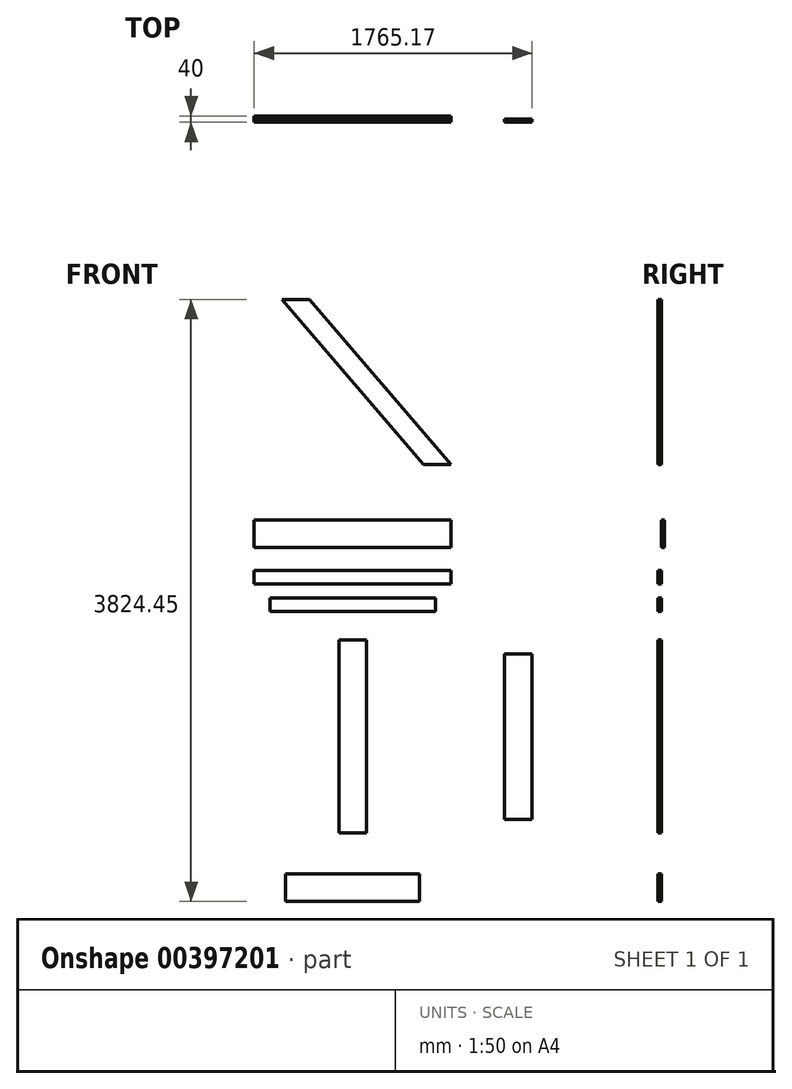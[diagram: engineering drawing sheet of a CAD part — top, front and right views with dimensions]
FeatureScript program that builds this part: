
annotation { "Feature Type Name" : "Feature", "Feature Type Description" : "" }
export const myFeature = defineFeature(function(context is Context, id is Id, definition is map)
    precondition{}
    {
        {
            var Q0;
            Q0=qCreatedBy(makeId("Front.planeOp"),FACE);
            var sketch = newSketch(context, id + "F0", { "sketchPlane" : qUnion([Q0])});
            skLineSegment(sketch, "E0.bottom", {"start": v(625, 87.5) * mm, "end": v(-625, 87.5) * mm});
            skLineSegment(sketch, "E0.top", {"start": v(625, -87.5) * mm, "end": v(-625, -87.5) * mm});
            skLineSegment(sketch, "E0.left", {"start": v(625, 87.5) * mm, "end": v(625, -87.5) * mm});
            skLineSegment(sketch, "E0.right", {"start": v(-625, 87.5) * mm, "end": v(-625, -87.5) * mm});
            skPoint(sketch, "E0.middle", {"position": v(0, 0) * mm});
            skSolve(sketch);
        }
        {
            var Q0;
            Q0 = qSketchRegion(id + "F0", true);
            extrude(context, id + "F1", {"entities" : qUnion([Q0]), "depth" : 20 * mm});
        }
        {
            var Q0;
            Q0=makeQuery(id+"F1.opExtrude","CAP_FACE",FACE,{"disambiguationData":[OSD([sQuery(id+"F0.wireOp",EDGE,"E0.bottom"),sQuery(id+"F0.wireOp",EDGE,"E0.top"),sQuery(id+"F0.wireOp",EDGE,"E0.left"),sQuery(id+"F0.wireOp",EDGE,"E0.right")])],"isStart":false});
            var sketch = newSketch(context, id + "F2", { "sketchPlane" : qUnion([Q0])});
            skLineSegment(sketch, "E1.bottom", {"start": v(625, -232.76) * mm, "end": v(-625, -232.76) * mm});
            skLineSegment(sketch, "E1.top", {"start": v(625, -320.26) * mm, "end": v(-625, -320.26) * mm});
            skLineSegment(sketch, "E1.left", {"start": v(625, -232.76) * mm, "end": v(625, -320.26) * mm});
            skLineSegment(sketch, "E1.right", {"start": v(-625, -232.76) * mm, "end": v(-625, -320.26) * mm});
            skPoint(sketch, "E1.middle", {"position": v(0, -276.5) * mm});
            skLineSegment(sketch, "E2.bottom", {"start": v(525, -407.33) * mm, "end": v(-525, -407.33) * mm});
            skLineSegment(sketch, "E2.top", {"start": v(525, -494.83) * mm, "end": v(-525, -494.83) * mm});
            skLineSegment(sketch, "E2.left", {"start": v(525, -407.33) * mm, "end": v(525, -494.83) * mm});
            skLineSegment(sketch, "E2.right", {"start": v(-525, -407.33) * mm, "end": v(-525, -494.83) * mm});
            skPoint(sketch, "E2.middle", {"position": v(0, -451.08) * mm});
            skPoint(sketch, "E2.middle.positionSnap0", {"position": v(0, -320.26) * mm});
            skPoint(sketch, "E2.centerSnap0", {"position": v(0, -320.26) * mm});
            skSolve(sketch);
        }
        {
            var Q0;
            Q0=makeQuery(id+"F2.imprint","IMPRINT",FACE,{"disambiguationData":[TD([[makeQuery(id+"F2.imprint","IMPRINT",EDGE,{"derivedFrom":sQuery(id+"F2.wireOp",EDGE,"E1.bottom")}),1.0]])]});
            var Q1;
            Q1=makeQuery(id+"F2.imprint","IMPRINT",FACE,{"disambiguationData":[TD([[makeQuery(id+"F2.imprint","IMPRINT",EDGE,{"derivedFrom":sQuery(id+"F2.wireOp",EDGE,"E2.bottom")}),1.0]])]});
            extrude(context, id + "F3", {"entities" : qUnion([Q0, Q1]), "depth" : 20 * mm});
        }
        {
            var Q0;
            Q0=makeQuery(id+"F1.opExtrude","CAP_FACE",FACE,{"disambiguationData":[OSD([sQuery(id+"F0.wireOp",EDGE,"E0.bottom"),sQuery(id+"F0.wireOp",EDGE,"E0.top"),sQuery(id+"F0.wireOp",EDGE,"E0.left"),sQuery(id+"F0.wireOp",EDGE,"E0.right")])],"isStart":false});
            var sketch = newSketch(context, id + "F4", { "sketchPlane" : qUnion([Q0])});
            skLineSegment(sketch, "E3.bottom", {"start": v(-450, 438.15) * mm, "end": v(625, 438.15) * mm, "construction": true});
            skLineSegment(sketch, "E3.top", {"start": v(-450, 1488.15) * mm, "end": v(625, 1488.15) * mm, "construction": true});
            skLineSegment(sketch, "E3.left", {"start": v(-450, 438.15) * mm, "end": v(-450, 1488.15) * mm, "construction": true});
            skLineSegment(sketch, "E3.right", {"start": v(625, 438.15) * mm, "end": v(625, 1488.15) * mm, "construction": true});
            skLineSegment(sketch, "E4", {"start": v(-450, 1488.15) * mm, "end": v(450, 438.15) * mm});
            skLineSegment(sketch, "E5", {"start": v(450, 438.15) * mm, "end": v(625, 438.15) * mm});
            skLineSegment(sketch, "E6", {"start": v(625, 438.15) * mm, "end": v(-275, 1488.15) * mm});
            skLineSegment(sketch, "E7", {"start": v(-275, 1488.15) * mm, "end": v(-450, 1488.15) * mm});
            skSolve(sketch);
        }
        {
            var Q0;
            Q0 = qSketchRegion(id + "F4", true);
            extrude(context, id + "F5", {"entities" : qUnion([Q0]), "depth" : 20 * mm});
        }
        {
            var Q0;
            Q0=makeQuery(id+"F1.opExtrude","CAP_FACE",FACE,{"disambiguationData":[OSD([sQuery(id+"F0.wireOp",EDGE,"E0.bottom"),sQuery(id+"F0.wireOp",EDGE,"E0.top"),sQuery(id+"F0.wireOp",EDGE,"E0.left"),sQuery(id+"F0.wireOp",EDGE,"E0.right")])],"isStart":false});
            var sketch = newSketch(context, id + "F6", { "sketchPlane" : qUnion([Q0])});
            skLineSegment(sketch, "E8.bottom", {"start": v(87.5, -1900.83) * mm, "end": v(-87.5, -1900.83) * mm});
            skLineSegment(sketch, "E8.top", {"start": v(87.5, -675.83) * mm, "end": v(-87.5, -675.83) * mm});
            skLineSegment(sketch, "E8.left", {"start": v(87.5, -1900.83) * mm, "end": v(87.5, -675.83) * mm});
            skLineSegment(sketch, "E8.right", {"start": v(-87.5, -1900.83) * mm, "end": v(-87.5, -675.83) * mm});
            skPoint(sketch, "E8.middle", {"position": v(0, -1288.33) * mm});
            skLineSegment(sketch, "E9.bottom", {"start": v(425, -2161.3) * mm, "end": v(-425, -2161.3) * mm});
            skLineSegment(sketch, "E9.top", {"start": v(425, -2336.3) * mm, "end": v(-425, -2336.3) * mm});
            skLineSegment(sketch, "E9.left", {"start": v(425, -2161.3) * mm, "end": v(425, -2336.3) * mm});
            skLineSegment(sketch, "E9.right", {"start": v(-425, -2161.3) * mm, "end": v(-425, -2336.3) * mm});
            skPoint(sketch, "E9.middle", {"position": v(0, -2248.8) * mm});
            skPoint(sketch, "E9.middle.positionSnap0", {"position": v(0, -1900.83) * mm});
            skPoint(sketch, "E9.centerSnap0", {"position": v(0, -1900.83) * mm});
            skLineSegment(sketch, "E10.bottom", {"start": v(1140.17, -763.33) * mm, "end": v(965.17, -763.33) * mm});
            skLineSegment(sketch, "E10.top", {"start": v(1140.17, -1813.33) * mm, "end": v(965.17, -1813.33) * mm});
            skLineSegment(sketch, "E10.left", {"start": v(1140.17, -763.33) * mm, "end": v(1140.17, -1813.33) * mm});
            skLineSegment(sketch, "E10.right", {"start": v(965.17, -763.33) * mm, "end": v(965.17, -1813.33) * mm});
            skPoint(sketch, "E10.middle", {"position": v(1052.67, -1288.33) * mm});
            skSolve(sketch);
        }
        {
            var Q0;
            Q0 = qSketchRegion(id + "F6", true);
            extrude(context, id + "F7", {"entities" : qUnion([Q0]), "depth" : 20 * mm});
        }
    });
